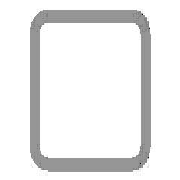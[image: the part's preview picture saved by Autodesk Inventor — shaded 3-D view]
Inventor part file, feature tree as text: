
AUTODESK INVENTOR PART (.ipt)
format: ipt  version: 2023 (Build 270158000, 158)  size: 215,040 bytes
history: native  units: mm (DEFAULTED — no unit token found)
features: other x18, sketch x5, extrude x3, plane x1
ambient origin geometry x8: Origin, YZ Plane, XZ Plane, XY Plane, X Axis, Y Axis, Z Axis, Center Point
bodies: Solid1 (feature_tree)
feature tree (27):
  parser-record x1  (decoder bookkeeping rows leaked as tree rows — omitted from the tree; the rows remain in map.json)
  other  "Driven Length"
  other  "Płaszczyzna początkowa"
  other  "Płaszczyzna końcowa"
  extrude  "Bryła"  TaperAngle=0.0deg  [1 undecoded]
  other  "Płaszczyzna konstrukcyjna4"
  other  "Podział1"
  other  "Płaszczyzna konstrukcyjna5"
  other  "Podział2"
  other  "Płaszczyzna konstrukcyjna6"
  other  "Płaszczyzna konstrukcyjna7"
  other  "Płaszczyzna konstrukcyjna8"
  extrude  "Wyciągnięcie proste2"  Depth=20.0mm
  other  "Utwórz kombinację1"
  other  "Płaszczyzna konstrukcyjna9"
  other  "Płaszczyzna konstrukcyjna10"
  other  "Płaszczyzna konstrukcyjna11"
  extrude  "Wyciągnięcie proste3"  Depth=20.0mm
  other  "Utwórz kombinację2"
  sketch  "Szkic"
  sketch  "Sketch3"  dims[d3=740.0mm d4=0.0mm]
  plane  "Work Plane3"
  sketch  "Sketch4"  dims[d7=4.0mm d10=40.0mm d11=40.0mm d12=3.2mm d13=-20.0mm d14=720.0mm d15=20.0mm d16=20.0mm d17=90.0deg d18=740.0mm d19=0.13mm d20=0.0mm d21=0.13mm d22=0.0mm]
  sketch  "Szkic5"
  other  "Bryła2"
  sketch  "Szkic6"
  other  "Bryła3"
note: 1 required parameter value undecoded (feature->parameter linkage not recoverable at this tier; creation-order binding heuristic only, values carry confidence <= 0.55)
